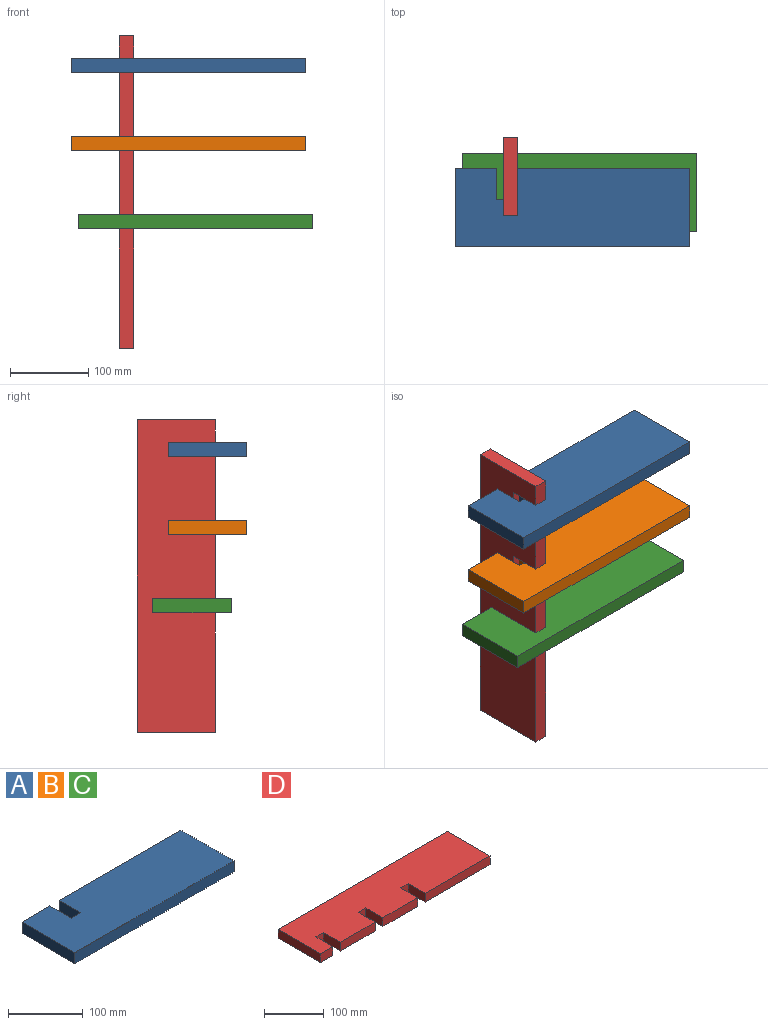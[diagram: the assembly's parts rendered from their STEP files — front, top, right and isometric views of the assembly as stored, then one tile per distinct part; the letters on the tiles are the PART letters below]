
ASSEMBLY  parts=4 mates=3
PART A: 10 faces, bbox 300x100x18 mm
  f0: plane 52.73x18mm, normal (0,1,0), area 949.1mm2, adj f1,f2,f3,f7
  f1: plane 300x100mm, normal (0,0,1), area 29280mm2, adj f0,f2,f4,f5,f6,f7,f8,f9
  f2: plane 100x18mm, normal (-1,0,0), area 1800mm2, adj f0,f1,f3,f5
  f3: plane 300x100mm, normal (0,0,-1), area 29280mm2, adj f0,f2,f4,f5,f6,f7,f8,f9
  f4: plane 100x18mm, normal (1,0,0), area 1800mm2, adj f1,f3,f5,f6
  f5: plane 300x18mm, normal (0,-1,0), area 5400mm2, adj f1,f2,f3,f4
  f6: plane 229.27x18mm, normal (0,1,0), area 4126.9mm2, adj f1,f3,f4,f9
  f7: plane 40x18mm, normal (1,0,0), area 720mm2, adj f0,f1,f3,f8
  f8: plane 18x18mm, normal (0,1,0), area 324mm2, adj f1,f3,f7,f9
  f9: plane 40x18mm, normal (-1,0,0), area 720mm2, adj f1,f3,f6,f8
PART B: same geometry as A
PART C: same geometry as A
PART D: 18 faces, bbox 400x100x18 mm
  f0: plane 40x18mm, normal (-1,0,0), area 720mm2, adj f1,f15,f16,f17
  f1: plane 152.79x18mm, normal (0,-1,0), area 2750.2mm2, adj f0,f2,f16,f17
  f2: plane 100x18mm, normal (1,0,0), area 1800mm2, adj f1,f3,f16,f17
  f3: plane 400x18mm, normal (0,1,0), area 7200mm2, adj f2,f4,f16,f17
  f4: plane 100x18mm, normal (-1,0,0), area 1800mm2, adj f3,f5,f16,f17
  f5: plane 29.21x18mm, normal (0,-1,0), area 525.8mm2, adj f4,f6,f16,f17
  f6: plane 40x18mm, normal (1,0,0), area 720mm2, adj f5,f7,f16,f17
  f7: plane 18x18mm, normal (0,-1,0), area 324mm2, adj f6,f8,f16,f17
  f8: plane 40x18mm, normal (-1,0,0), area 720mm2, adj f7,f9,f16,f17
  f9: plane 82x18mm, normal (0,-1,0), area 1476mm2, adj f8,f10,f16,f17
  f10: plane 40x18mm, normal (1,0,0), area 720mm2, adj f9,f11,f16,f17
  f11: plane 18x18mm, normal (0,-1,0), area 324mm2, adj f10,f12,f16,f17
  f12: plane 40x18mm, normal (-1,0,0), area 720mm2, adj f11,f13,f16,f17
  f13: plane 82x18mm, normal (0,-1,0), area 1476mm2, adj f12,f14,f16,f17
  f14: plane 40x18mm, normal (1,0,0), area 720mm2, adj f13,f15,f16,f17
  f15: plane 18x18mm, normal (0,-1,0), area 324mm2, adj f0,f14,f16,f17
  f16: plane 400x100mm, normal (0,0,1), area 37840mm2, adj f0,f1,f2,f3,f4,f5,f6,f7
  f17: plane 400x100mm, normal (0,0,-1), area 37840mm2, adj f0,f1,f2,f3,f4,f5,f6,f7
PLACE A t=(-80.33,-29.12,196.88)mm
PLACE B t=(-80.33,-29.12,96.88)mm
PLACE C t=(-71.33,-9.12,-3.12)mm
PLACE D rot(axis=(0,1,0),90deg) t=(-232.17,-33.36,-70.97)mm
MATE fastened B.f1 <-> D.f10  axis (0,0,1) through (-223.17,-69.12,107.26)mm
MATE fastened A.f1 <-> D.f6  axis (0,0,1) through (-223.17,-69.12,207.26)mm
MATE fastened C.f1 <-> D.f14  axis (0,0,1) through (-214.17,-49.12,7.26)mm
